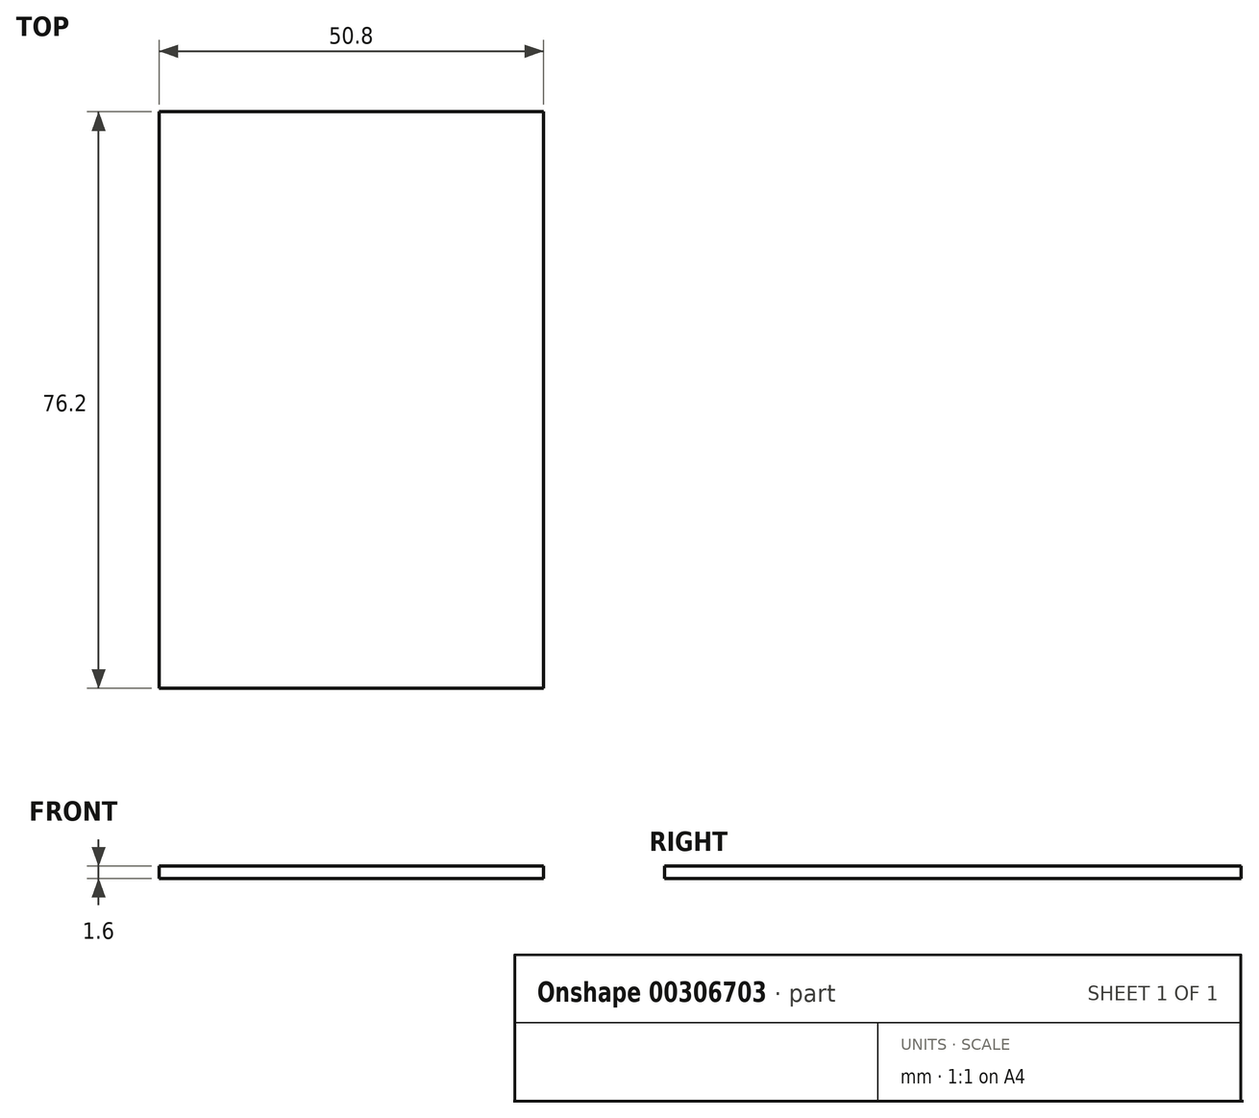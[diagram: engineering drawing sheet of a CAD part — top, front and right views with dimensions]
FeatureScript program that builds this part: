
annotation { "Feature Type Name" : "Feature", "Feature Type Description" : "" }
export const myFeature = defineFeature(function(context is Context, id is Id, definition is map)
    precondition{}
    {
        {
            var Q0;
            Q0=qCreatedBy(makeId("Top.planeOp"),FACE);
            var sketch = newSketch(context, id + "F0", { "sketchPlane" : qUnion([Q0])});
            skLineSegment(sketch, "E0.bottom", {"start": v(25.4, 38.1) * mm, "end": v(-25.4, 38.1) * mm});
            skLineSegment(sketch, "E0.top", {"start": v(25.4, -38.1) * mm, "end": v(-25.4, -38.1) * mm});
            skLineSegment(sketch, "E0.left", {"start": v(25.4, 38.1) * mm, "end": v(25.4, -38.1) * mm});
            skLineSegment(sketch, "E0.right", {"start": v(-25.4, 38.1) * mm, "end": v(-25.4, -38.1) * mm});
            skPoint(sketch, "E0.middle", {"position": v(0, 0) * mm});
            skSolve(sketch);
        }
        {
            var Q0;
            Q0=makeQuery(id+"F0.imprint","IMPRINT",FACE,{"disambiguationData":[TD([[makeQuery(id+"F0.imprint","IMPRINT",EDGE,{"derivedFrom":sQuery(id+"F0.wireOp",EDGE,"E0.bottom")}),1.0]])]});
            extrude(context, id + "F1", {"entities" : qUnion([Q0]), "depth" : 1.6 * mm});
        }
    });
